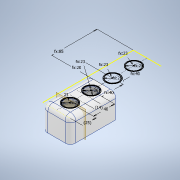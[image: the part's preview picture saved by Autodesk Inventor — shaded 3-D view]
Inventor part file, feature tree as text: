
AUTODESK INVENTOR PART (.ipt)
format: ipt  version: 2021 (Build 250183000, 183)  size: 4,087,296 bytes
history: native  units: in
note: dims shown in document units (in); Inventor stores cm internally (conversion verified against a paired STEP export)
features: extrude x10, other x9, fillet x3, sketch x1
ambient origin geometry x8: Origin, YZ Plane, XZ Plane, XY Plane, X Axis, Y Axis, Z Axis, Center Point
bodies: Body1 (feature_tree)
feature tree (23):
  extrude  "Base"  Depth=2.0472in
  other  "Top Indent Sketch"
  extrude  "Top"  Depth=1.7717in TaperAngle=0.0deg
  extrude  "Walls"  Depth=1.0236in
  fillet  "Outer"  Radius=1.0236in
  extrude  "Outer Wire"  Depth=1.0236in
  extrude  "Wall Holes"  Depth=1.0236in
  extrude  "Text"  Depth=1.5748in
  extrude  "Inner Sketch"  Depth=1.5748in
  fillet  "Inner Fillet"  Radius=1.5748in
  extrude  "halfer"  Depth=0.7087in TaperAngle=0.0deg
  extrude  "Top Indent"  Depth=0.315in
  other  "Wire Hole Plane"
  extrude  "Wire Hole"  Depth=0.315in
  fillet  "Fillet9"  Radius=0.2362in
  other  "Base Sketch"
  other  "Walls Sketch"
  other  "Outer Wire Sketch"
  other  "Wall Holes Sketch"
  other  "Text Sketch"
  other  "Inner Support Sketch"
  sketch  "Sketch25"  dims[d6=6.6929in d7=2.0472in d8=1.7717in d9=0.0in d10=1.0236in d11=1.0236in d12=1.0236in d13=1.0236in d14=1.5748in d15=1.5748in d16=1.5748in d19=0.7087in d20=0.0in d21=0.315in d22=0.315in d23=0.2362in d24=0.2362in d25=1.4567in d26=0.0in d27=0.9055in d28=0.9055in d29=0.9055in d30=0.9055in d31=0.7874in d32=3.3465in d33=1.5748in d35=0.9843in d36=0.3937in d38=0.3937in d39=0.0in d52=0.315in d55=0.1969in d56=0.0in d58=0.5512in d65=0.315in d66=0.1575in d67=0.1575in d68=0.315in d69=0.2774in d70=0.2774in d71=0.0499in d72=0.0499in d73=0.0787in d74=0.0in d77=0.6496in d81=0.9843in d82=0.0in d85=0.5906in d86=0.1575in d87=0.1575in d88=1.0236in d89=0.315in d90=0.1575in d92=0.0in d93=0.1181in d94=0.0in d95=0.1575in d96=0.6496in d143=0.0in d144=0.0in d155=3.3465in d156=0.0in d158=0.0709in d159=0.0in d162=0.2362in d163=0.0in d164=0.0in d165=0.1969in d166=0.2362in d167=0.0in d168=0.1969in d169=0.1969in d170=4.7244in d171=0.0in d172=3.3465in d173=1.0236in d174=0.0394in d175=1.2992in d44=0.0197in d45=0.0344in d46=0.0197in d47=0.0344in d48=0.0197in d49=0.0344in d59=0.0197in d60=0.0344in d61=0.0197in d62=0.0344in d176=0.0344in d177=0.0197in d178=0.0344in]
  other  "Wire Hole Sketch"
